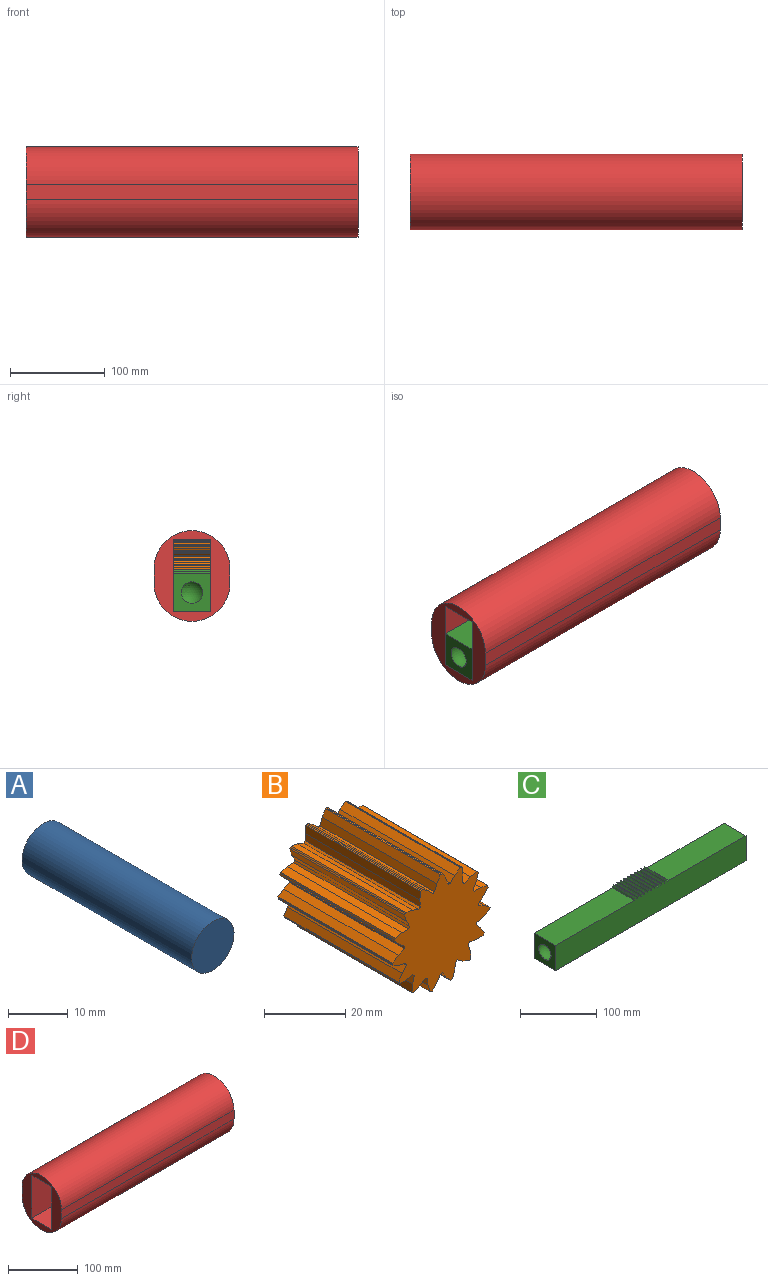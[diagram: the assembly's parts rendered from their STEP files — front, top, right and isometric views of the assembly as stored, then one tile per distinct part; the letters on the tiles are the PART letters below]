
ASSEMBLY  parts=4 mates=3
PART A: 3 faces, bbox 10x40x10 mm
  f0: cylinder r=5mm len=40mm, axis (0,1,0), area 1256.6mm2, adj f1,f2
  f1: plane 10x10mm, normal (0,-1,0), area 78.5mm2, adj f0
  f2: plane 10x10mm, normal (0,1,0), area 78.5mm2, adj f0
PART B: 107 faces, bbox 33.9x40x33.7 mm
  f0: cylinder r=13mm len=40mm, axis (0,1,0), area 29.3mm2, adj f1,f104,f105,f106
  f1: plane 40x2.1mm, normal (0.37,0,0.93), area 90.7mm2, adj f0,f2,f105,f106
  f2: plane 40x2.35mm, normal (0.21,0,0.98), area 96mm2, adj f1,f3,f105,f106
  f3: plane 40x0.27mm, normal (-0.74,0,0.68), area 14.7mm2, adj f2,f4,f105,f106
  f4: plane 40x0.28mm, normal (-0.75,0,0.66), area 14.7mm2, adj f3,f5,f105,f106
  f5: plane 40x2.28mm, normal (-0.95,0,-0.31), area 96mm2, adj f4,f6,f105,f106
  f6: plane 40x2mm, normal (-0.88,0,-0.47), area 90.7mm2, adj f5,f7,f105,f106
  f7: cylinder r=13mm len=40mm, axis (0,1,0), area 29.3mm2, adj f6,f8,f105,f106
  f8: plane 40x2.27mm, normal (-0.03,0,1), area 90.7mm2, adj f7,f9,f105,f106
  f9: plane 40x2.35mm, normal (-0.21,0,0.98), area 96mm2, adj f8,f10,f105,f106
  f10: plane 40x0.35mm, normal (-0.95,0,0.32), area 14.7mm2, adj f9,f11,f105,f106
  f11: plane 40x0.35mm, normal (-0.95,0,0.3), area 14.7mm2, adj f10,f12,f105,f106
  f12: plane 40x1.78mm, normal (-0.74,0,-0.67), area 96mm2, adj f11,f13,f105,f106
  f13: plane 40x1.79mm, normal (-0.62,0,-0.79), area 90.7mm2, adj f12,f14,f105,f106
  f14: cylinder r=13mm len=40mm, axis (0,1,0), area 29.3mm2, adj f13,f15,f105,f106
  f15: plane 40x2.04mm, normal (-0.44,0,0.9), area 90.7mm2, adj f14,f16,f105,f106
  f16: plane 40x1.94mm, normal (-0.59,0,0.81), area 96mm2, adj f15,f17,f105,f106
  f17: plane 40x0.37mm, normal (-1,0,-0.09), area 14.7mm2, adj f16,f18,f105,f106
  f18: plane 40x0.36mm, normal (-0.99,0,-0.12), area 14.7mm2, adj f17,f19,f105,f106
  f19: plane 40x2.19mm, normal (-0.41,0,-0.91), area 96mm2, adj f18,f20,f105,f106
  f20: plane 40x2.2mm, normal (-0.24,0,-0.97), area 90.7mm2, adj f19,f21,f105,f106
  f21: cylinder r=13mm len=40mm, axis (0,1,0), area 29.3mm2, adj f20,f22,f105,f106
  f22: plane 40x1.74mm, normal (-0.77,0,0.64), area 90.7mm2, adj f21,f23,f105,f106
  f23: plane 40x2.08mm, normal (-0.87,0,0.5), area 96mm2, adj f22,f24,f105,f106
  f24: plane 40x0.32mm, normal (-0.87,0,-0.49), area 14.7mm2, adj f23,f25,f105,f106
  f25: plane 40x0.32mm, normal (-0.86,0,-0.51), area 14.7mm2, adj f24,f26,f105,f106
  f26: plane 40x2.4mm, normal (0,0,-1), area 96mm2, adj f25,f27,f105,f106
  f27: plane 40x2.23mm, normal (0.17,0,-0.98), area 90.7mm2, adj f26,f28,f105,f106
  f28: cylinder r=13mm len=40mm, axis (0,1,0), area 29.3mm2, adj f27,f29,f105,f106
  f29: plane 40x2.18mm, normal (-0.96,0,0.28), area 90.7mm2, adj f28,f30,f105,f106
  f30: plane 40x2.39mm, normal (-0.99,0,0.1), area 96mm2, adj f29,f31,f105,f106
  f31: plane 40x0.29mm, normal (-0.6,0,-0.8), area 14.7mm2, adj f30,f32,f105,f106
  f32: plane 40x0.3mm, normal (-0.58,0,-0.82), area 14.7mm2, adj f31,f33,f105,f106
  f33: plane 40x2.19mm, normal (0.41,0,-0.91), area 96mm2, adj f32,f34,f105,f106
  f34: plane 40x1.88mm, normal (0.56,0,-0.83), area 90.7mm2, adj f33,f35,f105,f106
  f35: cylinder r=13mm len=40mm, axis (0,1,0), area 29.3mm2, adj f34,f36,f105,f106
  f36: plane 40x2.25mm, normal (-0.99,0,-0.14), area 90.7mm2, adj f35,f37,f105,f106
  f37: plane 40x2.28mm, normal (-0.95,0,-0.31), area 96mm2, adj f36,f38,f105,f106
  f38: plane 40x0.36mm, normal (-0.22,0,-0.98), area 14.7mm2, adj f37,f39,f105,f106
  f39: plane 40x0.36mm, normal (-0.2,0,-0.98), area 14.7mm2, adj f38,f40,f105,f106
  f40: plane 40x1.78mm, normal (0.74,0,-0.67), area 96mm2, adj f39,f41,f105,f106
  f41: plane 40x1.92mm, normal (0.85,0,-0.53), area 90.7mm2, adj f40,f42,f105,f106
  f42: cylinder r=13mm len=40mm, axis (0,1,0), area 29.3mm2, adj f41,f43,f105,f106
  f43: plane 40x1.92mm, normal (-0.85,0,-0.53), area 90.7mm2, adj f42,f44,f105,f106
  f44: plane 40x1.78mm, normal (-0.74,0,-0.67), area 96mm2, adj f43,f45,f105,f106
  f45: plane 40x0.36mm, normal (0.2,0,-0.98), area 14.7mm2, adj f44,f46,f105,f106
  f46: plane 40x0.36mm, normal (0.22,0,-0.98), area 14.7mm2, adj f45,f47,f105,f106
  f47: plane 40x2.28mm, normal (0.95,0,-0.31), area 96mm2, adj f46,f48,f105,f106
  f48: plane 40x2.25mm, normal (0.99,0,-0.14), area 90.7mm2, adj f47,f49,f105,f106
  f49: cylinder r=13mm len=40mm, axis (0,1,0), area 29.3mm2, adj f48,f50,f105,f106
  f50: plane 40x1.88mm, normal (-0.56,0,-0.83), area 90.7mm2, adj f49,f51,f105,f106
  f51: plane 40x2.19mm, normal (-0.41,0,-0.91), area 96mm2, adj f50,f52,f105,f106
  f52: plane 40x0.3mm, normal (0.58,0,-0.82), area 14.7mm2, adj f51,f53,f105,f106
  f53: plane 40x0.29mm, normal (0.6,0,-0.8), area 14.7mm2, adj f52,f54,f105,f106
  f54: plane 40x2.39mm, normal (0.99,0,0.1), area 96mm2, adj f53,f55,f105,f106
  f55: plane 40x2.18mm, normal (0.96,0,0.28), area 90.7mm2, adj f54,f56,f105,f106
  f56: cylinder r=13mm len=40mm, axis (0,1,0), area 29.3mm2, adj f55,f57,f105,f106
  f57: plane 40x2.23mm, normal (-0.17,0,-0.98), area 90.7mm2, adj f56,f58,f105,f106
  f58: plane 40x2.4mm, normal (0,0,-1), area 96mm2, adj f57,f59,f105,f106
  f59: plane 40x0.32mm, normal (0.86,0,-0.51), area 14.7mm2, adj f58,f60,f105,f106
  f60: plane 40x0.32mm, normal (0.87,0,-0.49), area 14.7mm2, adj f59,f61,f105,f106
  f61: plane 40x2.08mm, normal (0.87,0,0.5), area 96mm2, adj f60,f62,f105,f106
  f62: plane 40x1.74mm, normal (0.77,0,0.64), area 90.7mm2, adj f61,f63,f105,f106
  f63: cylinder r=13mm len=40mm, axis (0,1,0), area 29.3mm2, adj f62,f64,f105,f106
  f64: plane 40x2.2mm, normal (0.24,0,-0.97), area 90.7mm2, adj f63,f65,f105,f106
  f65: plane 40x2.19mm, normal (0.41,0,-0.91), area 96mm2, adj f64,f66,f105,f106
  f66: plane 40x0.36mm, normal (0.99,0,-0.12), area 14.7mm2, adj f65,f67,f105,f106
  f67: plane 40x0.37mm, normal (1,0,-0.09), area 14.7mm2, adj f66,f68,f105,f106
  f68: plane 40x1.94mm, normal (0.59,0,0.81), area 96mm2, adj f67,f69,f105,f106
  f69: plane 40x2.04mm, normal (0.44,0,0.9), area 90.7mm2, adj f68,f70,f105,f106
  f70: cylinder r=13mm len=40mm, axis (0,1,0), area 29.3mm2, adj f69,f71,f105,f106
  f71: plane 40x1.79mm, normal (0.62,0,-0.79), area 90.7mm2, adj f70,f72,f105,f106
  f72: plane 40x1.78mm, normal (0.74,0,-0.67), area 96mm2, adj f71,f73,f105,f106
  f73: plane 40x0.35mm, normal (0.95,0,0.3), area 14.7mm2, adj f72,f74,f105,f106
  f74: plane 40x0.35mm, normal (0.95,0,0.32), area 14.7mm2, adj f73,f75,f105,f106
  f75: plane 40x2.35mm, normal (0.21,0,0.98), area 96mm2, adj f74,f76,f105,f106
  f76: plane 40x2.27mm, normal (0.03,0,1), area 90.7mm2, adj f75,f77,f105,f106
  f77: cylinder r=13mm len=40mm, axis (0,1,0), area 29.3mm2, adj f76,f78,f105,f106
  f78: plane 40x2mm, normal (0.88,0,-0.47), area 90.7mm2, adj f77,f79,f105,f106
  f79: plane 40x2.28mm, normal (0.95,0,-0.31), area 96mm2, adj f78,f80,f105,f106
  f80: plane 40x0.28mm, normal (0.75,0,0.66), area 14.7mm2, adj f79,f81,f105,f106
  f81: plane 40x0.27mm, normal (0.74,0,0.68), area 14.7mm2, adj f80,f82,f105,f106
  f82: plane 40x2.35mm, normal (-0.21,0,0.98), area 96mm2, adj f81,f83,f105,f106
  f83: plane 40x2.1mm, normal (-0.37,0,0.93), area 90.7mm2, adj f82,f84,f105,f106
  f84: cylinder r=13mm len=40mm, axis (0,1,0), area 29.3mm2, adj f83,f85,f105,f106
  f85: plane 40x2.26mm, normal (1,0,-0.07), area 90.7mm2, adj f84,f86,f105,f106
  f86: plane 40x2.39mm, normal (0.99,0,0.11), area 96mm2, adj f85,f87,f105,f106
  f87: plane 40x0.33mm, normal (0.42,0,0.91), area 14.7mm2, adj f86,f88,f105,f106
  f88: plane 40x0.34mm, normal (0.4,0,0.92), area 14.7mm2, adj f87,f89,f105,f106
  f89: plane 40x1.94mm, normal (-0.59,0,0.81), area 96mm2, adj f88,f90,f105,f106
  f90: plane 40x1.63mm, normal (-0.72,0,0.69), area 90.7mm2, adj f89,f91,f105,f106
  f91: cylinder r=13mm len=40mm, axis (0,1,0), area 29.3mm2, adj f90,f92,f105,f106
  f92: plane 40x2.13mm, normal (0.94,0,0.34), area 90.7mm2, adj f91,f93,f105,f106
  f93: plane 40x2.08mm, normal (0.87,0,0.5), area 96mm2, adj f92,f94,f105,f106
  f94: plane 40x0.37mm, normal (0.01,0,1), area 14.7mm2, adj f93,f95,f105,f106
  f95: plane 40x0.37mm, normal (-0.01,0,1), area 14.7mm2, adj f94,f96,f105,f106
  f96: plane 40x2.08mm, normal (-0.87,0,0.5), area 96mm2, adj f95,f97,f105,f106
  f97: plane 40x2.13mm, normal (-0.94,0,0.34), area 90.7mm2, adj f96,f98,f105,f106
  f98: cylinder r=13mm len=40mm, axis (0,1,0), area 29.3mm2, adj f97,f99,f105,f106
  f99: plane 40x1.63mm, normal (0.72,0,0.69), area 90.7mm2, adj f98,f100,f105,f106
  f100: plane 40x1.94mm, normal (0.59,0,0.81), area 96mm2, adj f99,f101,f105,f106
  f101: plane 40x0.34mm, normal (-0.4,0,0.92), area 14.7mm2, adj f100,f102,f105,f106
  f102: plane 40x0.33mm, normal (-0.42,0,0.91), area 14.7mm2, adj f101,f103,f105,f106
  f103: plane 40x2.39mm, normal (-0.99,0,0.11), area 96mm2, adj f102,f104,f105,f106
  f104: plane 40x2.26mm, normal (-1,0,-0.07), area 90.7mm2, adj f0,f103,f105,f106
  f105: plane 33.88x33.7mm, normal (0,-1,0), area 706.3mm2, adj f0,f1,f2,f3,f4,f5,f6,f7
  f106: plane 33.88x33.7mm, normal (0,1,0), area 706.3mm2, adj f0,f1,f2,f3,f4,f5,f6,f7
PART C: 68 faces, bbox 361x40x44.3 mm
  f0: plane 40x0.73mm, normal (0,0,1), area 29.3mm2, adj f1,f63,f64,f65
  f1: plane 40x2mm, normal (-0.86,0,0.52), area 93.4mm2, adj f0,f2,f64,f65
  f2: plane 40x2.31mm, normal (-0.94,0,0.34), area 98.5mm2, adj f1,f3,f64,f65
  f3: plane 144.33x40mm, normal (0,0,1), area 5773.1mm2, adj f2,f4,f64,f65
  f4: plane 40x40mm, normal (-1,0,0), area 1195.3mm2, adj f3,f5,f64,f65,f67
  f5: plane 350x40mm, normal (0,0,-1), area 14000mm2, adj f4,f6,f64,f65
  f6: plane 40x40mm, normal (1,0,0), area 1192.1mm2, adj f5,f7,f64,f65,f66
  f7: plane 144.33x40mm, normal (0,0,1), area 5773.1mm2, adj f6,f8,f64,f65
  f8: plane 40x2.31mm, normal (0.94,0,0.34), area 98.5mm2, adj f7,f9,f64,f65
  f9: plane 40x2mm, normal (0.86,0,0.52), area 93.4mm2, adj f8,f10,f64,f65
  f10: plane 40x0.73mm, normal (0,0,1), area 29.3mm2, adj f9,f11,f64,f65
  f11: plane 40x2mm, normal (-0.86,0,0.52), area 93.4mm2, adj f10,f12,f64,f65
  f12: plane 40x2.31mm, normal (-0.94,0,0.34), area 98.5mm2, adj f11,f13,f64,f65
  f13: plane 40x1.46mm, normal (0,0,1), area 58.2mm2, adj f12,f14,f64,f65
  f14: plane 40x2.31mm, normal (0.94,0,0.34), area 98.5mm2, adj f13,f15,f64,f65
  f15: plane 40x2mm, normal (0.86,0,0.52), area 93.4mm2, adj f14,f16,f64,f65
  f16: plane 40x0.73mm, normal (0,0,1), area 29.3mm2, adj f15,f17,f64,f65
  f17: plane 40x2mm, normal (-0.86,0,0.52), area 93.4mm2, adj f16,f18,f64,f65
  f18: plane 40x2.31mm, normal (-0.94,0,0.34), area 98.5mm2, adj f17,f19,f64,f65
  f19: plane 40x1.46mm, normal (0,0,1), area 58.2mm2, adj f18,f20,f64,f65
  f20: plane 40x2.31mm, normal (0.94,0,0.34), area 98.5mm2, adj f19,f21,f64,f65
  f21: plane 40x2mm, normal (0.86,0,0.52), area 93.4mm2, adj f20,f22,f64,f65
  f22: plane 40x0.73mm, normal (0,0,1), area 29.3mm2, adj f21,f23,f64,f65
  f23: plane 40x2mm, normal (-0.86,0,0.52), area 93.4mm2, adj f22,f24,f64,f65
  f24: plane 40x2.31mm, normal (-0.94,0,0.34), area 98.5mm2, adj f23,f25,f64,f65
  f25: plane 40x1.46mm, normal (0,0,1), area 58.2mm2, adj f24,f26,f64,f65
  f26: plane 40x2.31mm, normal (0.94,0,0.34), area 98.5mm2, adj f25,f27,f64,f65
  f27: plane 40x2mm, normal (0.86,0,0.52), area 93.4mm2, adj f26,f28,f64,f65
  f28: plane 40x0.73mm, normal (0,0,1), area 29.3mm2, adj f27,f29,f64,f65
  f29: plane 40x2mm, normal (-0.86,0,0.52), area 93.4mm2, adj f28,f30,f64,f65
  f30: plane 40x2.31mm, normal (-0.94,0,0.34), area 98.5mm2, adj f29,f31,f64,f65
  f31: plane 40x1.46mm, normal (0,0,1), area 58.2mm2, adj f30,f32,f64,f65
  f32: plane 40x2.31mm, normal (0.94,0,0.34), area 98.5mm2, adj f31,f33,f64,f65
  f33: plane 40x2mm, normal (0.86,0,0.52), area 93.4mm2, adj f32,f34,f64,f65
  f34: plane 40x0.73mm, normal (0,0,1), area 29.3mm2, adj f33,f35,f64,f65
  f35: plane 40x2mm, normal (-0.86,0,0.52), area 93.4mm2, adj f34,f36,f64,f65
  f36: plane 40x2.31mm, normal (-0.94,0,0.34), area 98.5mm2, adj f35,f37,f64,f65
  f37: plane 40x1.46mm, normal (0,0,1), area 58.2mm2, adj f36,f38,f64,f65
  f38: plane 40x2.31mm, normal (0.94,0,0.34), area 98.5mm2, adj f37,f39,f64,f65
  f39: plane 40x2mm, normal (0.86,0,0.52), area 93.4mm2, adj f38,f40,f64,f65
  f40: plane 40x0.73mm, normal (0,0,1), area 29.3mm2, adj f39,f41,f64,f65
  f41: plane 40x2mm, normal (-0.86,0,0.52), area 93.4mm2, adj f40,f42,f64,f65
  f42: plane 40x2.31mm, normal (-0.94,0,0.34), area 98.5mm2, adj f41,f43,f64,f65
  f43: plane 40x1.46mm, normal (0,0,1), area 58.2mm2, adj f42,f44,f64,f65
  f44: plane 40x2.31mm, normal (0.94,0,0.34), area 98.5mm2, adj f43,f45,f64,f65
  f45: plane 40x2mm, normal (0.86,0,0.52), area 93.4mm2, adj f44,f46,f64,f65
  f46: plane 40x0.73mm, normal (0,0,1), area 29.3mm2, adj f45,f47,f64,f65
  f47: plane 40x2mm, normal (-0.86,0,0.52), area 93.4mm2, adj f46,f48,f64,f65
  f48: plane 40x2.31mm, normal (-0.94,0,0.34), area 98.5mm2, adj f47,f49,f64,f65
  f49: plane 40x1.46mm, normal (0,0,1), area 58.2mm2, adj f48,f50,f64,f65
  f50: plane 40x2.31mm, normal (0.94,0,0.34), area 98.5mm2, adj f49,f51,f64,f65
  f51: plane 40x2mm, normal (0.86,0,0.52), area 93.4mm2, adj f50,f52,f64,f65
  f52: plane 40x0.73mm, normal (0,0,1), area 29.3mm2, adj f51,f53,f64,f65
  f53: plane 40x2mm, normal (-0.86,0,0.52), area 93.4mm2, adj f52,f54,f64,f65
  f54: plane 40x2.31mm, normal (-0.94,0,0.34), area 98.5mm2, adj f53,f55,f64,f65
  f55: plane 40x1.46mm, normal (0,0,1), area 58.2mm2, adj f54,f56,f64,f65
  f56: plane 40x2.31mm, normal (0.94,0,0.34), area 98.5mm2, adj f55,f57,f64,f65
  f57: plane 40x2mm, normal (0.86,0,0.52), area 93.4mm2, adj f56,f58,f64,f65
  f58: plane 40x0.73mm, normal (0,0,1), area 29.3mm2, adj f57,f59,f64,f65
  f59: plane 40x2mm, normal (-0.86,0,0.52), area 93.4mm2, adj f58,f60,f64,f65
  f60: plane 40x2.31mm, normal (-0.94,0,0.34), area 98.5mm2, adj f59,f61,f64,f65
  f61: plane 40x1.46mm, normal (0,0,1), area 58.2mm2, adj f60,f62,f64,f65
  f62: plane 40x2.31mm, normal (0.94,0,0.34), area 98.5mm2, adj f61,f63,f64,f65
  f63: plane 40x2mm, normal (0.86,0,0.52), area 93.4mm2, adj f0,f62,f64,f65
  f64: plane 350x44.31mm, normal (0,-1,0), area 14130.9mm2, adj f0,f1,f2,f3,f4,f5,f6,f7
  f65: plane 350x44.31mm, normal (0,1,0), area 14130.9mm2, adj f0,f1,f2,f3,f4,f5,f6,f7
  f66: sphere r=14.5mm, area 2137.9mm2, adj f6
  f67: sphere r=14.5mm, area 2143.1mm2, adj f4
PART D: 10 faces, bbox 350x80x95.5 mm
  f0: plane 350x15.5mm, normal (0,1,0), area 5425.5mm2, adj f1,f3,f4,f5
  f1: cylinder r=40mm len=350mm, axis (-1,0,0), area 43982.3mm2, adj f0,f2,f4,f5
  f2: plane 350x15.5mm, normal (0,-1,0), area 5425.5mm2, adj f1,f3,f4,f5
  f3: cylinder r=40mm len=350mm, axis (-1,0,0), area 43982.3mm2, adj f0,f2,f4,f5
  f4: plane 95.5x80mm, normal (1,0,0), area 3249.2mm2, adj f0,f1,f2,f3,f6,f7,f8,f9
  f5: plane 95.5x80mm, normal (-1,0,0), area 3249.2mm2, adj f0,f1,f2,f3,f6,f7,f8,f9
  f6: plane 350x75.44mm, normal (0,1,0), area 26402.7mm2, adj f4,f5,f7,f9
  f7: plane 350x40mm, normal (0,0,1), area 14000mm2, adj f4,f5,f6,f8
  f8: plane 350x75.44mm, normal (0,-1,0), area 26402.7mm2, adj f4,f5,f7,f9
  f9: plane 350x40mm, normal (0,0,-1), area 14000mm2, adj f4,f5,f6,f8
PLACE A t=(62.72,6.95,-38.97)mm
PLACE B t=(94.7,6.95,17.67)mm
PLACE C t=(97.94,6.95,17.61)mm
PLACE D t=(97.91,6.95,17.37)mm fixed
MATE planar C.f5 <-> D.f7  axis (0,0,-1) through (97.91,-13.05,-39.75)mm
MATE revolute B.f98 <-> A.f0  axis (0,-1,0) through (94.7,-33.05,17.67)mm
MATE fastened A.f0 <-> D.f6  axis (0,-1,0) through (94.7,-33.05,17.67)mm
